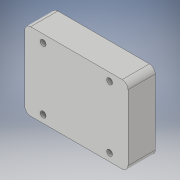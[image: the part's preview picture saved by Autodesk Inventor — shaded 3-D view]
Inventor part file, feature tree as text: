
AUTODESK INVENTOR PART (.ipt)
format: ipt  version: 2019 (Build 230136000, 136)  size: 112,640 bytes
history: native  units: in
note: dims shown in document units (in); Inventor stores cm internally (conversion verified against a paired STEP export)
features: sketch x2, extrude x1, hole x1, fillet x1
ambient origin geometry x8: Origin, YZ Plane, XZ Plane, XY Plane, X Axis, Y Axis, Z Axis, Center Point
bodies: Solid1 (feature_tree)
feature tree (5):
  extrude  "Extrusion1"  Depth=1.65in
  hole  "Hole1"  [1 undecoded]
  fillet  "Fillet1"  Radius=0.165in
  sketch  "Sketch1"  dims[d0=2.2in d1=1.65in]
  sketch  "Sketch2"  dims[d2=0.58in d3=0.0in d4=0.392in d5=0.165in d6=0.392in d7=0.165in d8=0.125in d9=0.75in d10=0.375in d11=0.25in d12=0.5635in d13=1.0in d14=0.8108in d15=0.125in]
note: 1 required parameter value undecoded (feature->parameter linkage not recoverable at this tier; creation-order binding heuristic only, values carry confidence <= 0.55)
